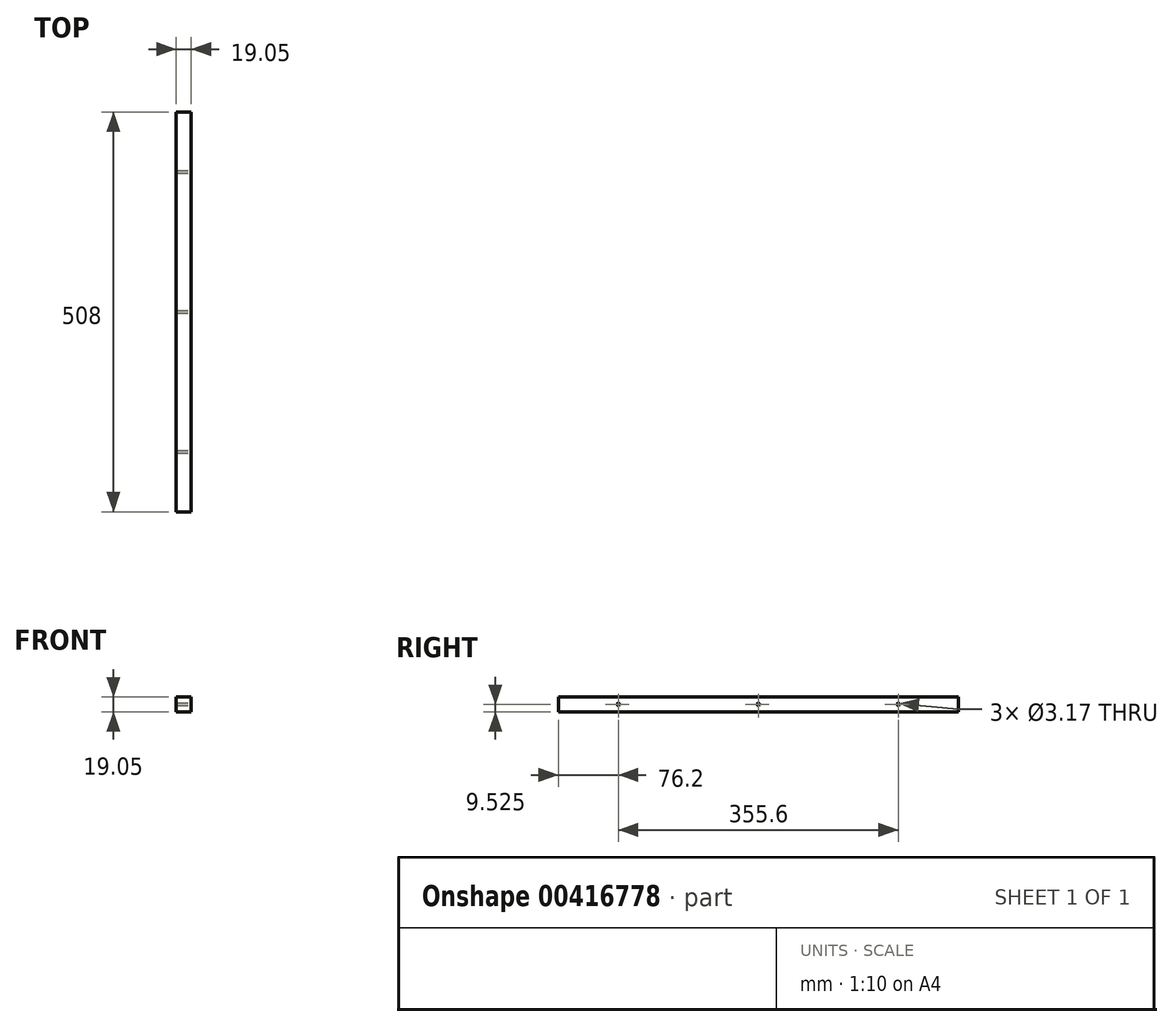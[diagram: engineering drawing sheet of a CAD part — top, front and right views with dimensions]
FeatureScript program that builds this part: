
annotation { "Feature Type Name" : "Feature", "Feature Type Description" : "" }
export const myFeature = defineFeature(function(context is Context, id is Id, definition is map)
    precondition{}
    {
        {
            var Q0;
            Q0=qCreatedBy(makeId("Front.planeOp"),FACE);
            var sketch = newSketch(context, id + "F0", { "sketchPlane" : qUnion([Q0])});
            skLineSegment(sketch, "E0.bottom", {"start": v(0, 0) * mm, "end": v(19.05, 0) * mm});
            skLineSegment(sketch, "E0.top", {"start": v(0, 19.05) * mm, "end": v(19.05, 19.05) * mm});
            skLineSegment(sketch, "E0.left", {"start": v(0, 0) * mm, "end": v(0, 19.05) * mm});
            skLineSegment(sketch, "E0.right", {"start": v(19.05, 0) * mm, "end": v(19.05, 19.05) * mm});
            skSolve(sketch);
        }
        {
            var Q0;
            Q0=makeQuery(id+"F0.imprint","IMPRINT",FACE,{"disambiguationData":[TD([[makeQuery(id+"F0.imprint","IMPRINT",EDGE,{"derivedFrom":sQuery(id+"F0.wireOp",EDGE,"E0.bottom")}),1.0]])]});
            extrude(context, id + "F1", {"entities" : qUnion([Q0]), "depth" : 508 * mm});
        }
        {
            var Q0;
            Q0=makeQuery(id+"F1.opExtrude","SWEPT_FACE",FACE,{"disambiguationData":[OSD([sQuery(id+"F0.wireOp",EDGE,"E0.right")])]});
            var sketch = newSketch(context, id + "F2", { "sketchPlane" : qUnion([Q0])});
            skLineSegment(sketch, "E1", {"start": v(-508, 9.53) * mm, "end": v(0, 9.53) * mm, "construction": true});
            skCircle(sketch, "E2", {"center": v(-254, 9.53) * mm, "radius": 1.59 * mm});
            skCircle(sketch, "E3", {"center": v(-76.2, 9.53) * mm, "radius": 1.59 * mm});
            skCircle(sketch, "E4", {"center": v(-431.8, 9.52) * mm, "radius": 1.59 * mm});
            skSolve(sketch);
        }
        {
            var Q0;
            Q0 = qSketchRegion(id + "F2", true);
            extrude(context, id + "F3", {"entities" : qUnion([Q0]), "operationType" : NewBodyOperationType.REMOVE, "oppositeDirection" : true, "depth" : 25.4 * mm});
        }
    });
